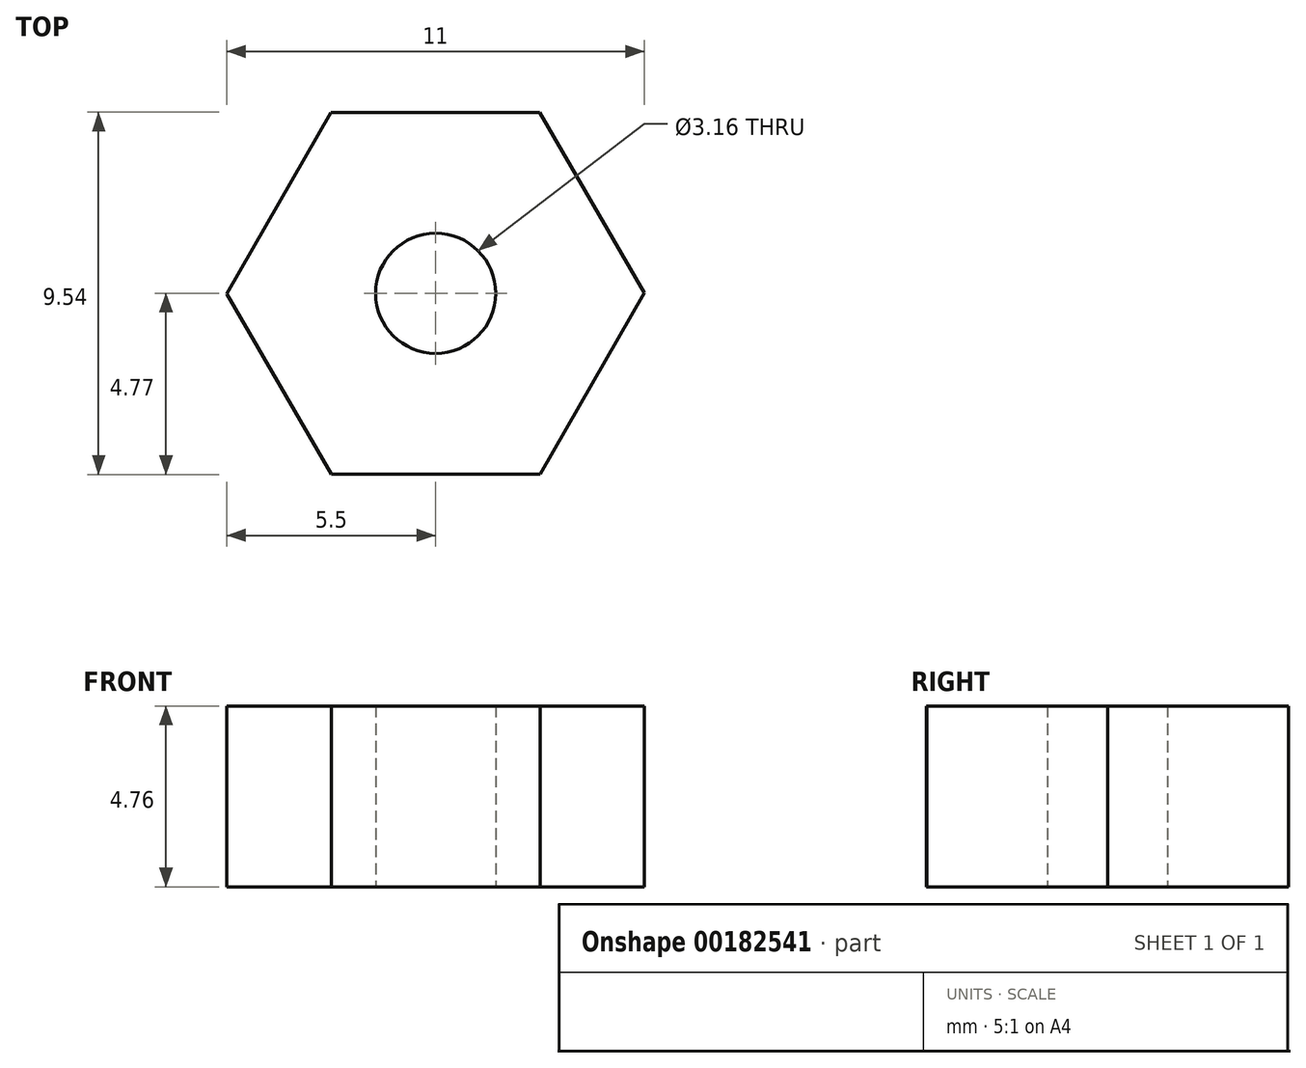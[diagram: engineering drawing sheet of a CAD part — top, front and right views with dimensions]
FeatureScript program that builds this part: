
annotation { "Feature Type Name" : "Feature", "Feature Type Description" : "" }
export const myFeature = defineFeature(function(context is Context, id is Id, definition is map)
    precondition{}
    {
        {
            var Q0;
            Q0=qCreatedBy(makeId("Top.planeOp"),FACE);
            var sketch = newSketch(context, id + "F0", { "sketchPlane" : qUnion([Q0])});
            skCircle(sketch, "E0.cCircle", {"center": v(0, 0) * mm, "radius": 4.76 * mm, "construction": true});
            skLineSegment(sketch, "E0.0", {"start": v(-5.5, -0.01) * mm, "end": v(-2.76, 4.76) * mm});
            skLineSegment(sketch, "E0.1", {"start": v(-2.76, 4.76) * mm, "end": v(2.74, 4.77) * mm});
            skLineSegment(sketch, "E0.2", {"start": v(2.74, 4.77) * mm, "end": v(5.5, 0.01) * mm});
            skLineSegment(sketch, "E0.3", {"start": v(5.5, 0.01) * mm, "end": v(2.76, -4.76) * mm});
            skLineSegment(sketch, "E0.4", {"start": v(2.76, -4.76) * mm, "end": v(-2.74, -4.77) * mm});
            skLineSegment(sketch, "E0.5", {"start": v(-2.74, -4.77) * mm, "end": v(-5.5, -0.01) * mm});
            skPoint(sketch, "E0.0.midPoint", {"position": v(-4.13, 2.37) * mm});
            skCircle(sketch, "E1", {"center": v(0, 0) * mm, "radius": 1.58 * mm});
            skSolve(sketch);
        }
        {
            var Q0;
            Q0 = qSketchRegion(id + "F0", true);
            extrude(context, id + "F1", {"entities" : qUnion([Q0]), "depth" : 4.76 * mm});
        }
    });
